# Revit family: NBS_DudleyIndustriesLimited_PprTwlDpnsrs_SlimLineRecessedPaperTowelDispenser
name_source: partatom
category: Specialty Equipment
revit_build: Autodesk Revit 2016 (Build: 20150220_1215(x64)
units: mm (PartAtom-declared; Revit-internal decimal feet)

## family parameters
Cut with Voids When Loaded = Yes
Host = Face
Part Type = Normal
Room Calculation Point = No
Round Connector Dimension = Use Diameter
Shared = No

## types (1)
- Slim Line Recessed Paper Towel Dispenser
    AssetType = Fixed
    BIMObjectName = NBS_DudleyIndustriesLimited_PaperTowelDispensers_SlimLineRecessedPaperTowelDispenser
    Category = Pr_40_70_22_62:Paper towel dispensers
    Default Elevation = 1000 mm  [stored 3.28084 ft]
    Description = Stylish satin stainless steel paper towel dispenser
    DurationUnit = year
    ExpectedLife = 20
    Features = Clean ergonomic design, Suitable for 100mm wall cavities, Durable stainless steel enclosure, Seam welded fabrication, Integral painted metal liner, Available as an individual unit or with Waste Bin and Warm Air Dryer, Will take either C of multi-fold interleaved paper towels
    Finish = Brushed stainless steel
    Form = Recessed, Wall mounted
    IfcExportAs = IfcFurnitureType
    IfcExportType = NOTDEFINED
    IntegralAccessories = Available as individual unit or with Waste Bin and Warm Air Dryer
    MainColor = Satin stainless steel
    ManufacturerName = Dudley Industries Limited
    ManufacturerURL = www.dudleyindustries.com
    Material = Brushed stainless steel
    MaterialsBody = 304 Stainless steel
    MaterialsColourAndFinish = Satin stainless steel
    ModelNumber = 92280SS
    ModelReference = Slim Line Recessed Paper Towel Dispenser
    NBSCertification = www.nationalbimlibrary.com/cert/1dudxbq2
    NBSDescription = Paper towel dispensers
    NBSReference = 45-35-72/344
    Name = PaperTowelDispensers_SlimLineRecessedPaperTowelDispenser_DudleyIndustriesLimited
    NominalDepth = 116 mm  [stored 0.380577 ft]
    NominalHeight = 579 mm  [stored 1.89961 ft]
    NominalLength = 382 mm  [stored 1.25328 ft]
    NominalWidth = 382 mm  [stored 1.25328 ft]
    Operation = Pull Out
    PaperTowelCapacity = Two packs
    ProductInformation = www.dudleyindustries.com/product/slim-line-recessed-paper-towel-dispenser/
    SanitaryDispenserMaterial = NBS_Concept
    Style = Paper Towel Dispenser
    SustainabilityPerformance = 100% Recycleable
    TowelType = Adjustable to take both C-fold and multi-fold interleaved paper towels
    TowelWidth = 230mm max
    Uniclass2015Code = Pr_40_70_22_62
    Uniclass2015Title = Paper towel dispensers
    Uniclass2015Version = Products v1.4
    Version = 3
    WarrantyDescription = Parts & Labour
    WarrantyDurationLabor = year
    WarrantyDurationParts = year
    WarrantyDurationUnit = year
    WarrantyGuarantorLabor = 10
    WarrantyGuarantorParts = 10
    Weight = 10.5 kg

note: [stored X ft] marks values corroborated as IEEE doubles in the binary element streams (Revit-internal decimal feet)

## geometry (parser evidence)
native form markers: Sweep x2
no freeform markers — native parametric forms only
